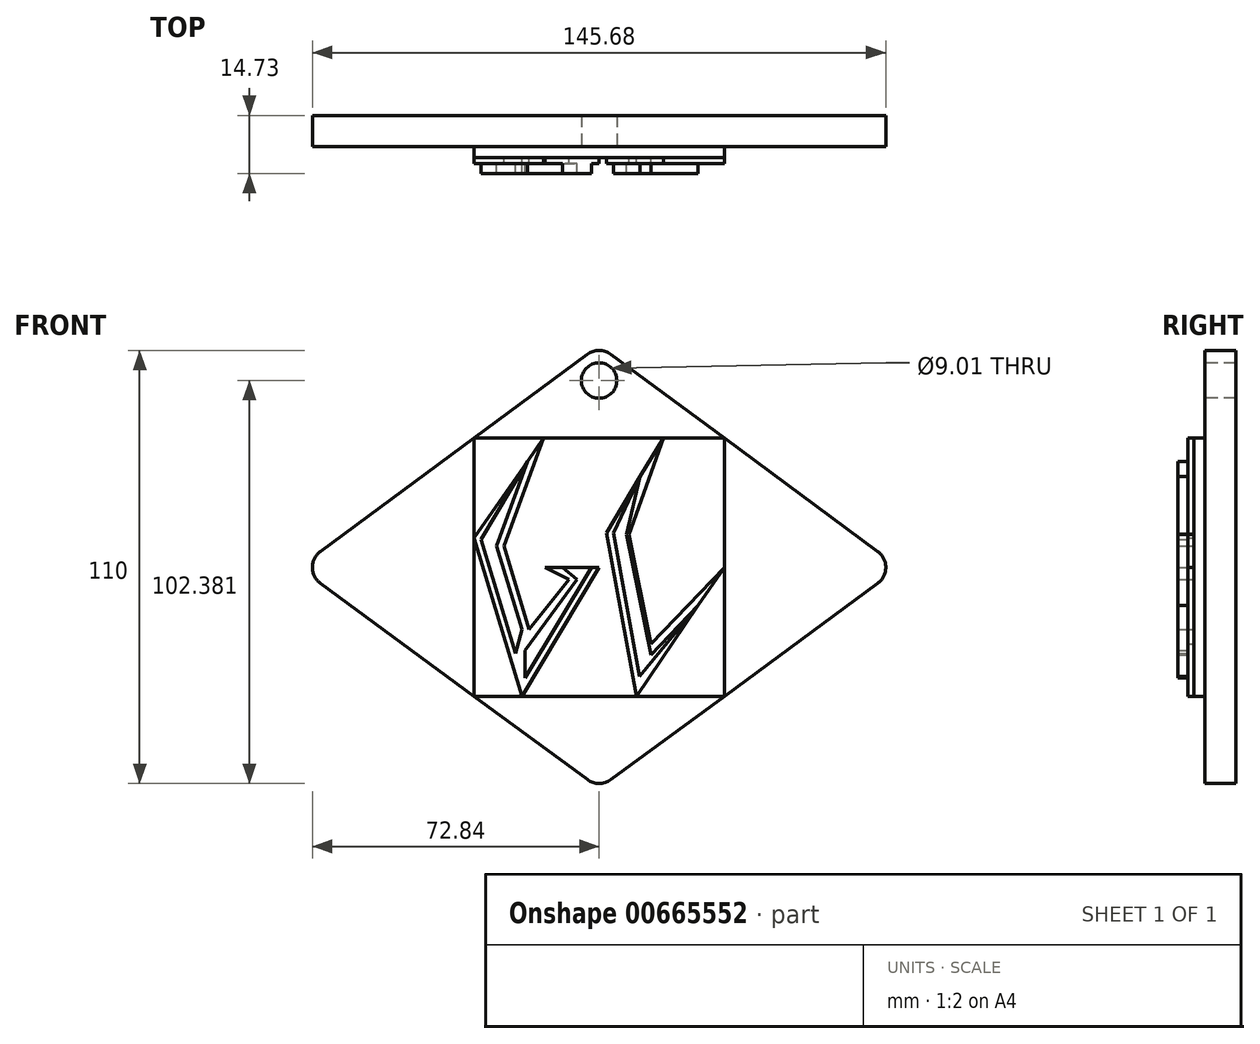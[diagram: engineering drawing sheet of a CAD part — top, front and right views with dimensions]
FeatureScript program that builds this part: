
annotation { "Feature Type Name" : "Feature", "Feature Type Description" : "" }
export const myFeature = defineFeature(function(context is Context, id is Id, definition is map)
    precondition{}
    {
        {
            var Q0;
            Q0=qCreatedBy(makeId("Front.planeOp"),FACE);
            var sketch = newSketch(context, id + "F0", { "sketchPlane" : qUnion([Q0])});
            skLineSegment(sketch, "E0", {"start": v(0, 56.32) * mm, "end": v(-76.32, 0) * mm});
            skLineSegment(sketch, "E1", {"start": v(-76.32, 0) * mm, "end": v(0, -56.14) * mm});
            skLineSegment(sketch, "E2", {"start": v(0, -56.14) * mm, "end": v(76.32, 0) * mm});
            skLineSegment(sketch, "E3", {"start": v(76.32, 0) * mm, "end": v(0, 56.32) * mm});
            skSolve(sketch);
        }
        {
            var Q0;
            Q0 = qSketchRegion(id + "F0", true);
            extrude(context, id + "F1", {"entities" : qUnion([Q0]), "depth" : 7.87 * mm, "offsetDistance" : 25.4 * mm});
        }
        {
            var Q0;
            Q0=makeQuery(id+"F1.opExtrude","CAP_FACE",FACE,{"disambiguationData":[OSD([sQuery(id+"F0.wireOp",EDGE,"E0"),sQuery(id+"F0.wireOp",EDGE,"E1"),sQuery(id+"F0.wireOp",EDGE,"E2"),sQuery(id+"F0.wireOp",EDGE,"E3")])],"isStart":false});
            var sketch = newSketch(context, id + "F2", { "sketchPlane" : qUnion([Q0])});
            skLineSegment(sketch, "E4", {"start": v(-31.8, 32.85) * mm, "end": v(-31.8, -32.74) * mm});
            skLineSegment(sketch, "E5", {"start": v(-31.8, -32.74) * mm, "end": v(31.8, -32.74) * mm});
            skLineSegment(sketch, "E6", {"start": v(31.8, -32.74) * mm, "end": v(31.8, 32.85) * mm});
            skLineSegment(sketch, "E7", {"start": v(31.8, 32.85) * mm, "end": v(-31.8, 32.85) * mm});
            skSolve(sketch);
        }
        {
            var Q0;
            Q0 = qSketchRegion(id + "F2", true);
            extrude(context, id + "F3", {"entities" : qUnion([Q0]), "operationType" : NewBodyOperationType.ADD, "endBound" : BoundingType.SYMMETRIC, "depth" : 5.6 * mm, "offsetDistance" : 25.4 * mm});
        }
        {
            var Q0;
            Q0=makeQuery(id+"F3.opExtrude","CAP_FACE",FACE,{"disambiguationData":[OSD([sQuery(id+"F2.wireOp",EDGE,"E4"),sQuery(id+"F2.wireOp",EDGE,"E5"),sQuery(id+"F2.wireOp",EDGE,"E6"),sQuery(id+"F2.wireOp",EDGE,"E7")])],"isStart":false});
            var sketch = newSketch(context, id + "F4", { "sketchPlane" : qUnion([Q0])});
            skLineSegment(sketch, "E8", {"start": v(-14.1, 32.85) * mm, "end": v(-31.8, 7.47) * mm});
            skLineSegment(sketch, "E9", {"start": v(-31.8, 7.47) * mm, "end": v(-19.63, -32.74) * mm});
            skLineSegment(sketch, "E10", {"start": v(-19.63, -32.74) * mm, "end": v(0, 0) * mm});
            skLineSegment(sketch, "E11", {"start": v(0, 0) * mm, "end": v(-13.73, 0) * mm});
            skLineSegment(sketch, "E12", {"start": v(-13.73, 0) * mm, "end": v(-7.65, -3.04) * mm});
            skLineSegment(sketch, "E13", {"start": v(-7.65, -3.04) * mm, "end": v(-17.8, -15.76) * mm});
            skLineSegment(sketch, "E14", {"start": v(-17.8, -15.76) * mm, "end": v(-24.2, 5.43) * mm});
            skLineSegment(sketch, "E15", {"start": v(-24.2, 5.43) * mm, "end": v(-14.1, 32.85) * mm});
            skSolve(sketch);
        }
        {
            var Q0;
            Q0=makeQuery(id+"F4.imprint","IMPRINT",FACE,{"disambiguationData":[TD([[makeQuery(id+"F4.imprint","IMPRINT",EDGE,{"derivedFrom":sQuery(id+"F4.wireOp",EDGE,"E8")}),1.0]])]});
            extrude(context, id + "F5", {"entities" : qUnion([Q0]), "operationType" : NewBodyOperationType.ADD, "endBound" : BoundingType.SYMMETRIC, "depth" : 3.05 * mm, "offsetDistance" : 25.4 * mm});
        }
        {
            var Q0;
            Q0=makeQuery(id+"F5.opExtrude","CAP_FACE",FACE,{"disambiguationData":[OSD([sQuery(id+"F4.wireOp",EDGE,"E8"),sQuery(id+"F4.wireOp",EDGE,"E9"),sQuery(id+"F4.wireOp",EDGE,"E10"),sQuery(id+"F4.wireOp",EDGE,"E11"),sQuery(id+"F4.wireOp",EDGE,"E12"),sQuery(id+"F4.wireOp",EDGE,"E13"),sQuery(id+"F4.wireOp",EDGE,"E14"),sQuery(id+"F4.wireOp",EDGE,"E15")])],"isStart":false});
            var sketch = newSketch(context, id + "F6", { "sketchPlane" : qUnion([Q0])});
            skLineSegment(sketch, "E16", {"start": v(-18.22, 26.94) * mm, "end": v(-29.96, 7.1) * mm});
            skLineSegment(sketch, "E17", {"start": v(-29.96, 7.1) * mm, "end": v(-21.2, -21.82) * mm});
            skLineSegment(sketch, "E18", {"start": v(-21.2, -21.82) * mm, "end": v(-19.63, -15.76) * mm});
            skLineSegment(sketch, "E19", {"start": v(-19.63, -15.76) * mm, "end": v(-26.05, 5.43) * mm});
            skLineSegment(sketch, "E20", {"start": v(-26.05, 5.43) * mm, "end": v(-18.22, 26.94) * mm});
            skLineSegment(sketch, "E21", {"start": v(-9.3, 0) * mm, "end": v(-1.94, 0) * mm});
            skLineSegment(sketch, "E22", {"start": v(-1.94, 0) * mm, "end": v(-18.8, -28.13) * mm});
            skLineSegment(sketch, "E23", {"start": v(-18.8, -28.13) * mm, "end": v(-18.8, -21.1) * mm});
            skLineSegment(sketch, "E24", {"start": v(-18.8, -21.1) * mm, "end": v(-5.62, -3.04) * mm});
            skLineSegment(sketch, "E25", {"start": v(-5.62, -3.04) * mm, "end": v(-9.3, 0) * mm});
            skSolve(sketch);
        }
        {
            var Q0;
            Q0 = qSketchRegion(id + "F6", true);
            extrude(context, id + "F7", {"entities" : qUnion([Q0]), "operationType" : NewBodyOperationType.ADD, "endBound" : BoundingType.SYMMETRIC, "depth" : 5.08 * mm, "offsetDistance" : 25.4 * mm});
        }
        {
            var Q0;
            {var subQ0=sQuery(id+"F2.wireOp",EDGE,"E7");var subQ1=sQuery(id+"F2.wireOp",EDGE,"E6");var subQ2=sQuery(id+"F2.wireOp",EDGE,"E5");var subQ3=makeQuery(id+"F3.opExtrude","CAP_FACE",FACE,{"disambiguationData":[OSD([sQuery(id+"F2.wireOp",EDGE,"E4"),subQ2,subQ1,subQ0])],"isStart":false});Q0=makeQuery(id+"F5.boolean.opBoolean","SPLIT",FACE,{"disambiguationData":[TD([subQ3,makeQuery(id+"F3.opExtrude","SWEPT_FACE",FACE,{"disambiguationData":[OSD([subQ2])]}),makeQuery(id+"F3.opExtrude","SWEPT_FACE",FACE,{"disambiguationData":[OSD([subQ1])]}),makeQuery(id+"F3.opExtrude","SWEPT_FACE",FACE,{"disambiguationData":[OSD([subQ0])]}),makeQuery(id+"F5.opExtrude","SWEPT_FACE",FACE,{"disambiguationData":[OSD([sQuery(id+"F4.wireOp",EDGE,"E8")])]}),makeQuery(id+"F5.opExtrude","SWEPT_FACE",FACE,{"disambiguationData":[OSD([sQuery(id+"F4.wireOp",EDGE,"E9")])]}),makeQuery(id+"F5.opExtrude","SWEPT_FACE",FACE,{"disambiguationData":[OSD([sQuery(id+"F4.wireOp",EDGE,"E10")])]}),makeQuery(id+"F5.opExtrude","SWEPT_FACE",FACE,{"disambiguationData":[OSD([sQuery(id+"F4.wireOp",EDGE,"E11")])]}),makeQuery(id+"F5.opExtrude","SWEPT_FACE",FACE,{"disambiguationData":[OSD([sQuery(id+"F4.wireOp",EDGE,"E12")])]}),makeQuery(id+"F5.opExtrude","SWEPT_FACE",FACE,{"disambiguationData":[OSD([sQuery(id+"F4.wireOp",EDGE,"E13")])]}),makeQuery(id+"F5.opExtrude","SWEPT_FACE",FACE,{"disambiguationData":[OSD([sQuery(id+"F4.wireOp",EDGE,"E14")])]}),makeQuery(id+"F5.opExtrude","SWEPT_FACE",FACE,{"disambiguationData":[OSD([sQuery(id+"F4.wireOp",EDGE,"E15")])]})])],"derivedFrom":subQ3});}
            var sketch = newSketch(context, id + "F8", { "sketchPlane" : qUnion([Q0])});
            skLineSegment(sketch, "E26", {"start": v(16.32, 32.85) * mm, "end": v(1.87, 8.76) * mm});
            skLineSegment(sketch, "E27", {"start": v(1.87, 8.76) * mm, "end": v(9.5, -32.74) * mm});
            skLineSegment(sketch, "E28", {"start": v(9.5, -32.74) * mm, "end": v(31.8, 0) * mm});
            skLineSegment(sketch, "E29", {"start": v(31.8, 0) * mm, "end": v(13.18, -19.45) * mm});
            skLineSegment(sketch, "E30", {"start": v(13.18, -19.45) * mm, "end": v(7.65, 8.39) * mm});
            skLineSegment(sketch, "E31", {"start": v(7.65, 8.39) * mm, "end": v(16.32, 32.85) * mm});
            skSolve(sketch);
        }
        {
            var Q0;
            Q0 = qSketchRegion(id + "F8", true);
            extrude(context, id + "F9", {"entities" : qUnion([Q0]), "operationType" : NewBodyOperationType.ADD, "endBound" : BoundingType.SYMMETRIC, "depth" : 3.05 * mm, "offsetDistance" : 25.4 * mm});
        }
        {
            var Q0;
            Q0=makeQuery(id+"F9.opExtrude","CAP_FACE",FACE,{"disambiguationData":[OSD([sQuery(id+"F8.wireOp",EDGE,"E26"),sQuery(id+"F8.wireOp",EDGE,"E27"),sQuery(id+"F8.wireOp",EDGE,"E28"),sQuery(id+"F8.wireOp",EDGE,"E29"),sQuery(id+"F8.wireOp",EDGE,"E30"),sQuery(id+"F8.wireOp",EDGE,"E31")])],"isStart":false});
            var sketch = newSketch(context, id + "F10", { "sketchPlane" : qUnion([Q0])});
            skLineSegment(sketch, "E32", {"start": v(10.44, 23.05) * mm, "end": v(3.6, 8.76) * mm});
            skLineSegment(sketch, "E33", {"start": v(3.6, 8.76) * mm, "end": v(10.3, -27.73) * mm});
            skLineSegment(sketch, "E34", {"start": v(10.3, -27.73) * mm, "end": v(25.18, -9.72) * mm});
            skPoint(sketch, "E34.endSnap0", {"position": v(22.5, -9.72) * mm});
            skLineSegment(sketch, "E35", {"start": v(25.18, -9.72) * mm, "end": v(13.18, -22.21) * mm});
            skLineSegment(sketch, "E36", {"start": v(13.18, -22.21) * mm, "end": v(6.95, 8.39) * mm});
            skPoint(sketch, "E36.endSnap0", {"position": v(6.95, -9.49) * mm});
            skLineSegment(sketch, "E37", {"start": v(6.95, 8.39) * mm, "end": v(10.44, 23.05) * mm});
            skSolve(sketch);
        }
        {
            var Q0;
            Q0 = qSketchRegion(id + "F10", true);
            extrude(context, id + "F11", {"entities" : qUnion([Q0]), "operationType" : NewBodyOperationType.ADD, "endBound" : BoundingType.SYMMETRIC, "depth" : 5.08 * mm, "offsetDistance" : 25.4 * mm});
        }
        {
            var Q0;
            Q0=makeQuery(id+"F1.opExtrude","SWEPT_EDGE",EDGE,{"disambiguationData":[OSD([sQuery(id+"F0.wireOp",EDGE,"E0"),sQuery(id+"F0.wireOp",EDGE,"E3")])]});
            var Q1;
            Q1=makeQuery(id+"F1.opExtrude","SWEPT_EDGE",EDGE,{"disambiguationData":[OSD([sQuery(id+"F0.wireOp",EDGE,"E2"),sQuery(id+"F0.wireOp",EDGE,"E3")])]});
            var Q2;
            Q2=makeQuery(id+"F1.opExtrude","SWEPT_EDGE",EDGE,{"disambiguationData":[OSD([sQuery(id+"F0.wireOp",EDGE,"E1"),sQuery(id+"F0.wireOp",EDGE,"E2")])]});
            var Q3;
            Q3=makeQuery(id+"F1.opExtrude","SWEPT_EDGE",EDGE,{"disambiguationData":[OSD([sQuery(id+"F0.wireOp",EDGE,"E0"),sQuery(id+"F0.wireOp",EDGE,"E1")])]});
            fillet(context, id + "F12", {"entities" : qUnion([Q0, Q1, Q2, Q3]), "radius" : 5.08 * mm, "tangentPropagation" : true, "allowEdgeOverflow" : false});
        }
        {
            var Q0;
            {var subQ0=sQuery(id+"F0.wireOp",EDGE,"E3");var subQ1=sQuery(id+"F0.wireOp",EDGE,"E0");var subQ2=makeQuery(id+"F1.opExtrude","CAP_FACE",FACE,{"disambiguationData":[OSD([subQ1,sQuery(id+"F0.wireOp",EDGE,"E1"),sQuery(id+"F0.wireOp",EDGE,"E2"),subQ0])],"isStart":false});Q0=makeQuery(id+"F3.boolean.opBoolean","SPLIT",FACE,{"disambiguationData":[TD([makeQuery(id+"F1.opExtrude","SWEPT_FACE",FACE,{"disambiguationData":[OSD([subQ1])]}),subQ2,makeQuery(id+"F1.opExtrude","SWEPT_FACE",FACE,{"disambiguationData":[OSD([subQ0])]}),makeQuery(id+"F3.opExtrude","SWEPT_FACE",FACE,{"disambiguationData":[OSD([sQuery(id+"F2.wireOp",EDGE,"E4")])]}),makeQuery(id+"F3.opExtrude","SWEPT_FACE",FACE,{"disambiguationData":[OSD([sQuery(id+"F2.wireOp",EDGE,"E6")])]}),makeQuery(id+"F3.opExtrude","SWEPT_FACE",FACE,{"disambiguationData":[OSD([sQuery(id+"F2.wireOp",EDGE,"E7")])]})])],"derivedFrom":subQ2});}
            var sketch = newSketch(context, id + "F13", { "sketchPlane" : qUnion([Q0])});
            skCircle(sketch, "E38", {"center": v(0, 47.47) * mm, "radius": 4.5 * mm});
            skSolve(sketch);
        }
        {
            var Q0;
            Q0 = qSketchRegion(id + "F13", true);
            extrude(context, id + "F14", {"entities" : qUnion([Q0]), "operationType" : NewBodyOperationType.REMOVE, "endBound" : BoundingType.THROUGH_ALL, "oppositeDirection" : true, "depth" : 25.4 * mm, "offsetDistance" : 25.4 * mm});
        }
    });
